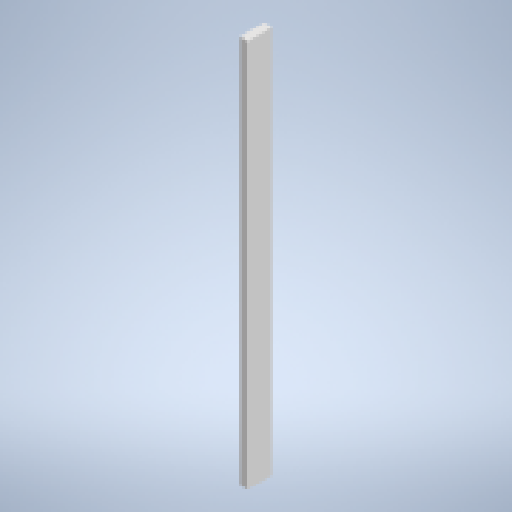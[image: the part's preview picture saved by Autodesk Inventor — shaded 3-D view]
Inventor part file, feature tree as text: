
AUTODESK INVENTOR PART (.ipt)
format: ipt  version: 2025.2 (Build 292293000, 293)  size: 133,632 bytes
history: native  units: in
note: dims shown in document units (in); Inventor stores cm internally (conversion verified against a paired STEP export)
features: extrude x1
ambient origin geometry x8: Origin, YZ Plane, XZ Plane, XY Plane, X Axis, Y Axis, Z Axis, Center Point
bodies: Solid1 (feature_tree)
feature tree (1):
  extrude  "Extrusion1"  Depth=1.0in
